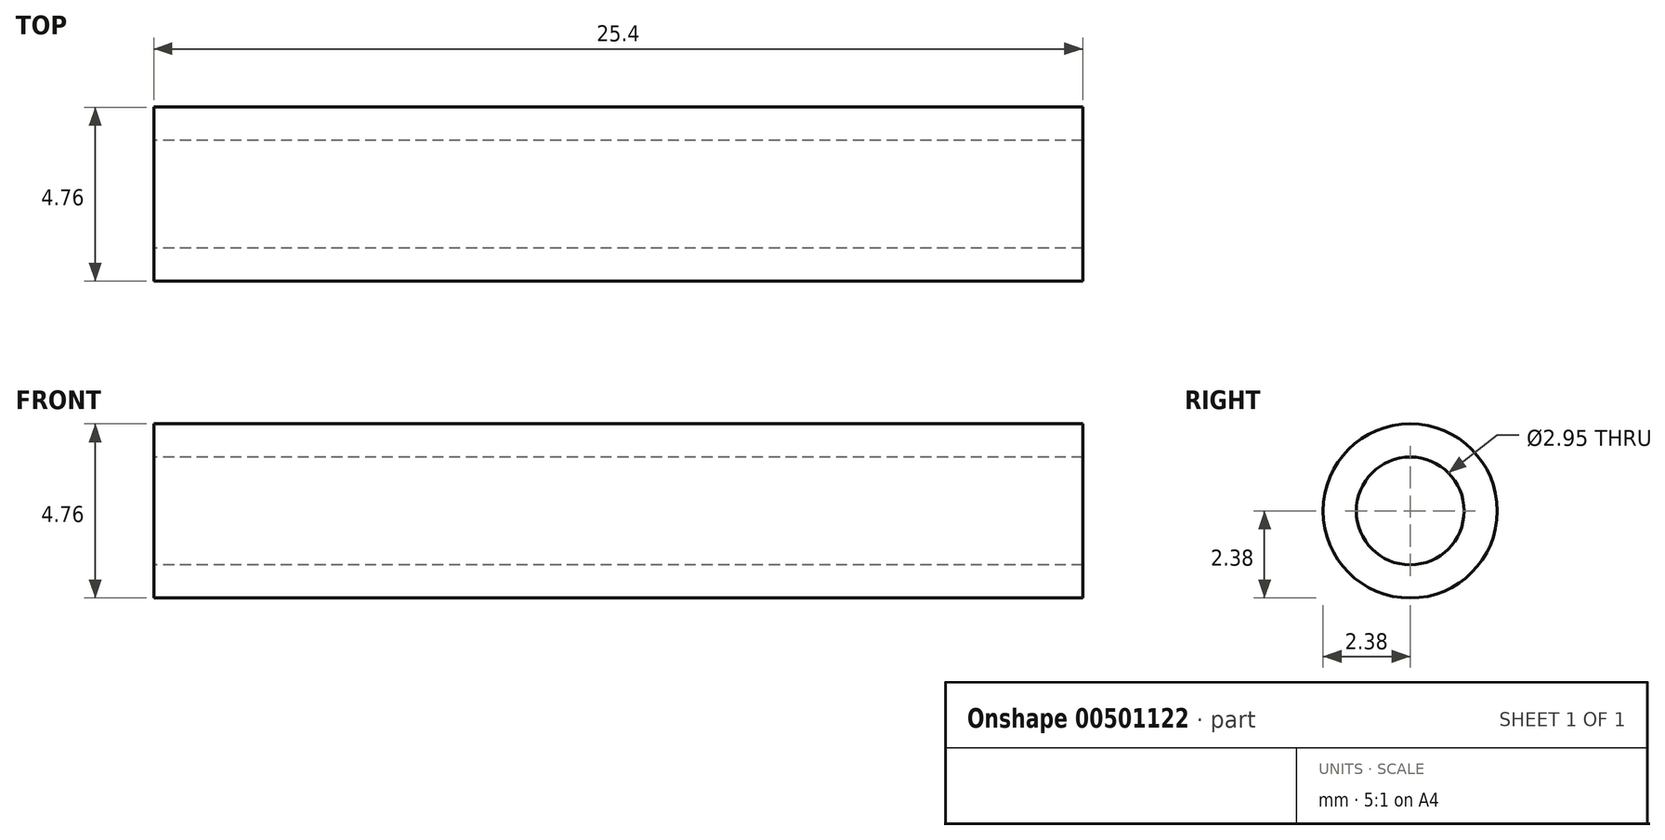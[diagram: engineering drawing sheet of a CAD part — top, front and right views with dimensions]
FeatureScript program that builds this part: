
annotation { "Feature Type Name" : "Feature", "Feature Type Description" : "" }
export const myFeature = defineFeature(function(context is Context, id is Id, definition is map)
    precondition{}
    {
        {
            var Q0;
            Q0=qCreatedBy(makeId("Right.planeOp"),FACE);
            var sketch = newSketch(context, id + "F0", { "sketchPlane" : qUnion([Q0])});
            skCircle(sketch, "E0", {"center": v(0, 0) * mm, "radius": 2.38 * mm});
            skCircle(sketch, "E1", {"center": v(0, 0) * mm, "radius": 1.47 * mm});
            skSolve(sketch);
        }
        {
            var Q0;
            Q0=qSketchRegion(id+"F0",true);
            extrude(context, id + "F1", {"entities" : qUnion([Q0]), "depth" : 25.4 * mm, "symmetric" : true});
        }
    });
